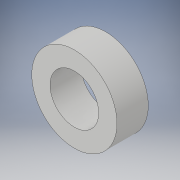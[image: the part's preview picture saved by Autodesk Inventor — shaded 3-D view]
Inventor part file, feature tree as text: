
AUTODESK INVENTOR PART (.ipt)
format: ipt  version: 2019 (Build 230136000, 136)  size: 101,888 bytes
history: native  units: mm
features: extrude x2, sketch x2
ambient origin geometry x8: Origin, YZ Plane, XZ Plane, XY Plane, X Axis, Y Axis, Z Axis, Center Point
bodies: Solid1 (feature_tree)
feature tree (4):
  extrude  "Extrusion1"  Depth=144.0mm TaperAngle=0.0deg
  extrude  "Extrusion2"  Depth=14.4mm TaperAngle=0.0deg
  sketch  "Sketch1"  dims[d0=392.0mm d1=144.0mm d2=0.0mm]
  sketch  "Sketch2"  dims[d3=224.0mm d4=14.4mm d5=0.0mm]
